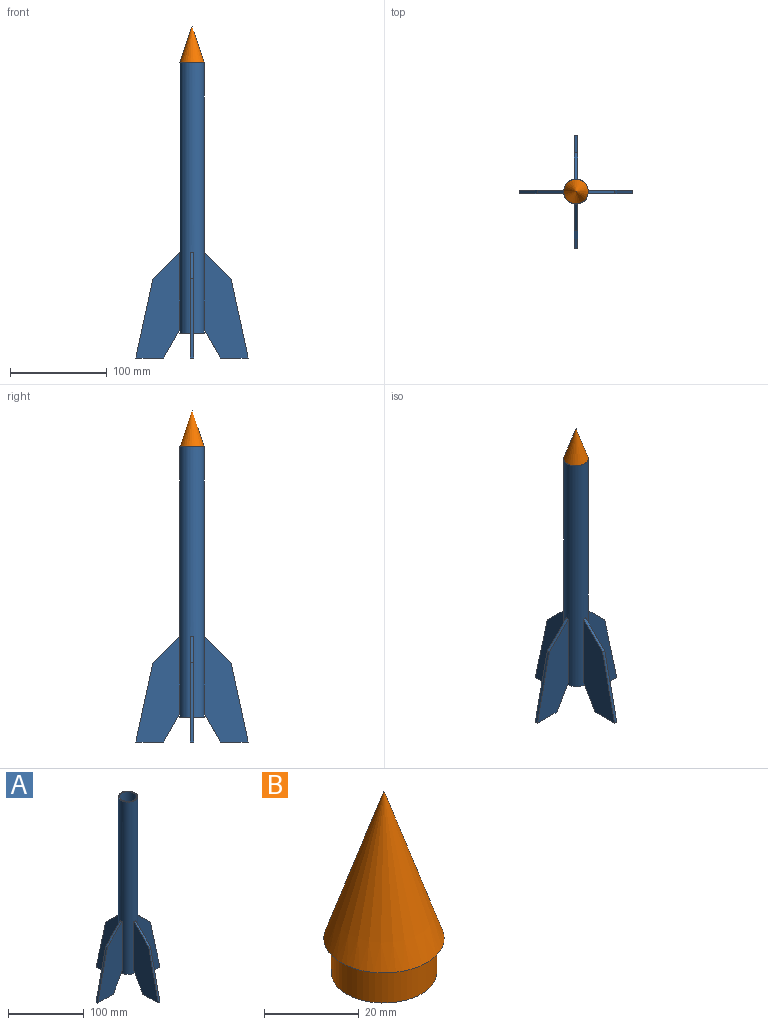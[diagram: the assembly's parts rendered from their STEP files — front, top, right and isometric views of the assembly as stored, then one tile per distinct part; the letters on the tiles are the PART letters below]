
ASSEMBLY  parts=2 mates=1
PART A: 28 faces, bbox 116.1x116.1x304.8 mm
  f0: cylinder r=12.7mm len=279.4mm, axis (0,0,-1), area 21274.8mm2, adj f1,f2,f3,f4,f5,f10,f11,f12
  f1: plane 25.4x25.4mm, normal (0,0,1), area 118.8mm2, adj f0,f26
  f2: plane 109.04x45.46mm, normal (1,0,0), area 3118.2mm2, adj f0,f4,f5,f6,f7
  f3: plane 109.04x45.46mm, normal (-1,0,0), area 3117.9mm2, adj f0,f4,f5,f6,f7
  f4: plane 29.6x16.64mm, normal (0,0.87,-0.49), area 108.2mm2, adj f0,f2,f3,f7
  f5: plane 27.66x27.37mm, normal (0,-0.7,0.71), area 124.2mm2, adj f0,f2,f3,f6
  f6: plane 81.67x17.8mm, normal (0,-0.98,0.21), area 267.5mm2, adj f2,f3,f5,f7
  f7: plane 28.82x3.2mm, normal (0,0,-1), area 92.2mm2, adj f2,f3,f4,f6
  f8: plane 28.82x3.2mm, normal (0,0,-1), area 92.2mm2, adj f9,f11,f12,f13
  f9: plane 81.67x17.8mm, normal (0,0.98,0.21), area 267.5mm2, adj f8,f10,f11,f12
  f10: plane 27.66x27.37mm, normal (0,0.7,0.71), area 124.2mm2, adj f0,f9,f11,f12
  f11: plane 109.04x45.46mm, normal (1,0,0), area 3117.9mm2, adj f0,f8,f9,f10,f13
  f12: plane 109.04x45.46mm, normal (-1,0,0), area 3118.2mm2, adj f0,f8,f9,f10,f13
  f13: plane 29.6x16.64mm, normal (0,-0.87,-0.49), area 108.2mm2, adj f0,f8,f11,f12
  f14: plane 28.82x3.2mm, normal (0,0,-1), area 92.2mm2, adj f15,f16,f17,f19
  f15: plane 81.67x17.8mm, normal (-0.98,0,0.21), area 267.5mm2, adj f14,f16,f17,f18
  f16: plane 109.04x45.46mm, normal (0,1,0), area 3117.9mm2, adj f0,f14,f15,f18,f19
  f17: plane 109.04x45.46mm, normal (0,-1,0), area 3118.2mm2, adj f0,f14,f15,f18,f19
  f18: plane 27.66x27.37mm, normal (-0.7,0,0.71), area 124.2mm2, adj f0,f15,f16,f17
  f19: plane 29.6x16.64mm, normal (0.87,0,-0.49), area 108.2mm2, adj f0,f14,f16,f17
  f20: plane 109.04x45.46mm, normal (0,1,0), area 3118.2mm2, adj f0,f22,f23,f24,f25
  f21: plane 109.04x45.46mm, normal (0,-1,0), area 3117.9mm2, adj f0,f22,f23,f24,f25
  f22: plane 29.6x16.64mm, normal (-0.87,0,-0.49), area 108.2mm2, adj f0,f20,f21,f25
  f23: plane 27.66x27.37mm, normal (0.7,0,0.71), area 124.2mm2, adj f0,f20,f21,f24
  f24: plane 81.67x17.8mm, normal (0.98,0,0.21), area 267.5mm2, adj f20,f21,f23,f25
  f25: plane 28.82x3.2mm, normal (0,0,-1), area 92.2mm2, adj f20,f21,f22,f24
  f26: cylinder r=11.11mm len=279.4mm, axis (0,0,1), area 19508.2mm2, adj f1,f27
  f27: plane 25.4x25.4mm, normal (0,0,-1), area 118.8mm2, adj f0,f26
PART B: 4 faces, bbox 25.4x25.4x47 mm
  f0: plane 25.4x25.4mm, normal (0,0,-1), area 118.8mm2, adj f1,f2
  f1: cone r=0mm half-angle=18.4deg, axis (0,0,-1), area 1602.3mm2, adj f0
  f2: cylinder r=11.11mm len=22.23mm, axis (0,0,1), area 620.7mm2, adj f0,f3
  f3: plane 22.23x22.23mm, normal (0,0,-1), area 387.9mm2, adj f2
PLACE A t=(-20.84,21.23,21.54)mm
PLACE B t=(-20.84,21.23,326.34)mm
MATE fastened B.f1 <-> A.f26  axis (0,0,-1) through (-20.84,21.23,326.34)mm
